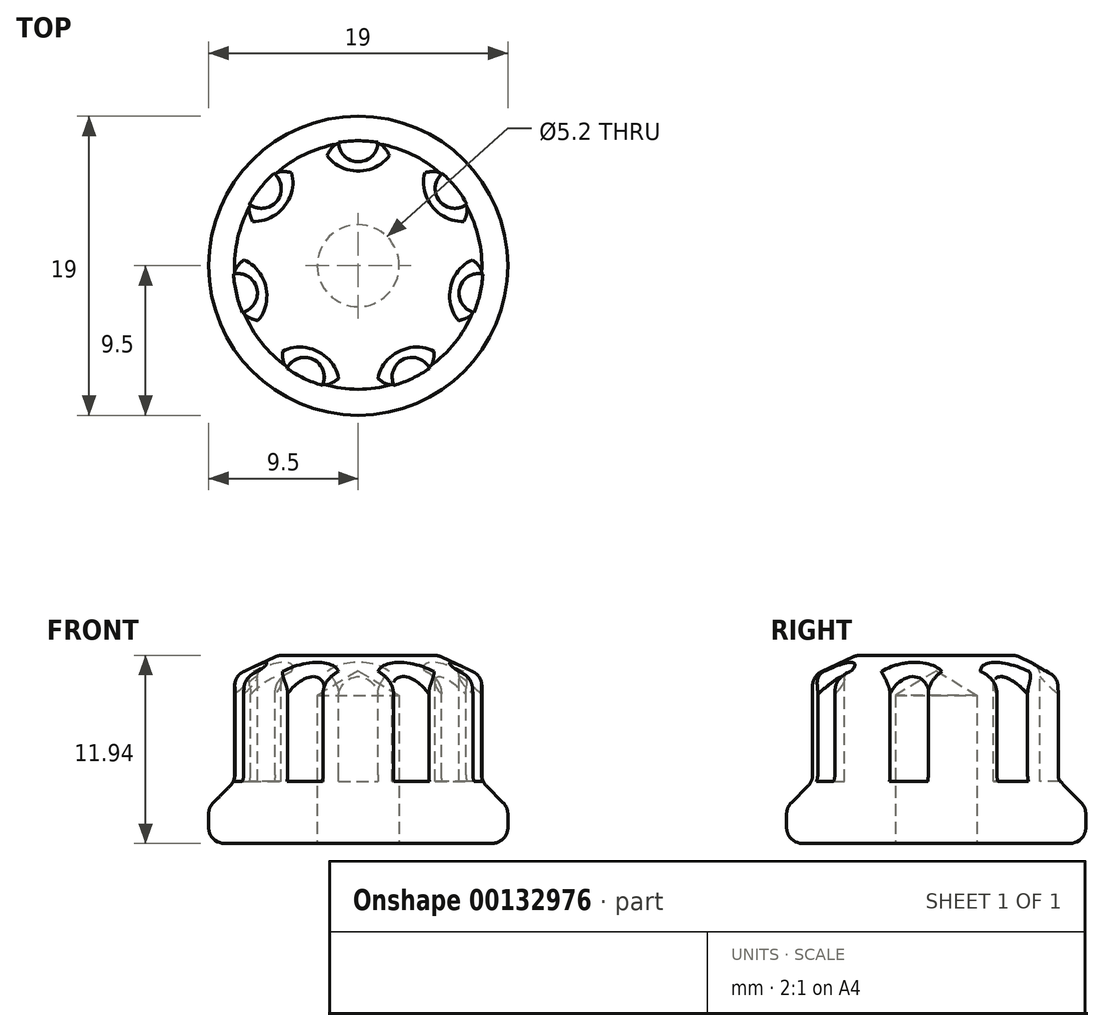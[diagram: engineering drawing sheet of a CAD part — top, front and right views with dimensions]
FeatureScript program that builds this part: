
annotation { "Feature Type Name" : "Feature", "Feature Type Description" : "" }
export const myFeature = defineFeature(function(context is Context, id is Id, definition is map)
    precondition{}
    {
        {
            var Q0;
            Q0=qCreatedBy(makeId("Front.planeOp"),FACE);
            var sketch = newSketch(context, id + "F0", { "sketchPlane" : qUnion([Q0])});
            skLineSegment(sketch, "E0", {"start": v(0, 0) * mm, "end": v(9.5, 0) * mm});
            skLineSegment(sketch, "E1", {"start": v(9.5, 0) * mm, "end": v(9.5, 2.29) * mm});
            skLineSegment(sketch, "E2", {"start": v(7.85, 3.94) * mm, "end": v(9.5, 2.29) * mm});
            skLineSegment(sketch, "E3", {"start": v(7.85, 3.94) * mm, "end": v(7.85, 10.65) * mm});
            skLineSegment(sketch, "E4", {"start": v(7.85, 10.65) * mm, "end": v(5.08, 11.94) * mm});
            skLineSegment(sketch, "E5", {"start": v(5.08, 11.94) * mm, "end": v(0, 11.94) * mm});
            skLineSegment(sketch, "E6", {"start": v(0, 11.94) * mm, "end": v(0, 0) * mm});
            skSolve(sketch);
        }
        {
            var Q0;
            Q0=makeQuery(id+"F0.imprint","IMPRINT",FACE,{"disambiguationData":[TD([[makeQuery(id+"F0.imprint","IMPRINT",EDGE,{"derivedFrom":sQuery(id+"F0.wireOp",EDGE,"E0")}),1.0]])]});
            var Q1;
            Q1=sQuery(id+"F0.wireOp",EDGE,"E6");
            revolve(context, id + "F1", {"entities" : qUnion([Q0]), "axis" : qUnion([Q1]), "revolveType" : RevolveType.FULL});
        }
        {
            var Q0;
            Q0=makeQuery(id+"F1.opRevolve","SWEPT_FACE",FACE,{"disambiguationData":[OSD([sQuery(id+"F0.wireOp",EDGE,"E5")])]});
            var sketch = newSketch(context, id + "F2", { "sketchPlane" : qUnion([Q0])});
            skCircle(sketch, "E7", {"center": v(0, 7.85) * mm, "radius": 1.25 * mm});
            skCircle(sketch, "E8.1.0", {"center": v(-6.14, 4.9) * mm, "radius": 1.25 * mm});
            skCircle(sketch, "E8.2.0", {"center": v(-7.65, -1.75) * mm, "radius": 1.25 * mm});
            skCircle(sketch, "E8.3.0", {"center": v(-3.4, -7.07) * mm, "radius": 1.25 * mm});
            skCircle(sketch, "E8.4.0", {"center": v(3.4, -7.07) * mm, "radius": 1.25 * mm});
            skCircle(sketch, "E8.5.0", {"center": v(7.65, -1.75) * mm, "radius": 1.25 * mm});
            skCircle(sketch, "E8.6.0", {"center": v(6.14, 4.9) * mm, "radius": 1.25 * mm});
            skPoint(sketch, "E8.center", {"position": v(0, 0) * mm});
            skSolve(sketch);
        }
        {
            var Q0;
            Q0=makeQuery(id+"F2.imprint","IMPRINT",FACE,{"disambiguationData":[TD([[makeQuery(id+"F2.imprint","IMPRINT",EDGE,{"derivedFrom":sQuery(id+"F2.wireOp",EDGE,"E8.2.0")}),1.0]])]});
            var Q1;
            Q1=makeQuery(id+"F2.imprint","IMPRINT",FACE,{"disambiguationData":[TD([[makeQuery(id+"F2.imprint","IMPRINT",EDGE,{"derivedFrom":sQuery(id+"F2.wireOp",EDGE,"E8.1.0")}),1.0]])]});
            var Q2;
            Q2=makeQuery(id+"F2.imprint","IMPRINT",FACE,{"disambiguationData":[TD([[makeQuery(id+"F2.imprint","IMPRINT",EDGE,{"derivedFrom":sQuery(id+"F2.wireOp",EDGE,"E7")}),1.0]])]});
            var Q3;
            Q3=makeQuery(id+"F2.imprint","IMPRINT",FACE,{"disambiguationData":[TD([[makeQuery(id+"F2.imprint","IMPRINT",EDGE,{"derivedFrom":sQuery(id+"F2.wireOp",EDGE,"E8.6.0")}),1.0]])]});
            var Q4;
            Q4=makeQuery(id+"F2.imprint","IMPRINT",FACE,{"disambiguationData":[TD([[makeQuery(id+"F2.imprint","IMPRINT",EDGE,{"derivedFrom":sQuery(id+"F2.wireOp",EDGE,"E8.5.0")}),1.0]])]});
            var Q5;
            Q5=makeQuery(id+"F2.imprint","IMPRINT",FACE,{"disambiguationData":[TD([[makeQuery(id+"F2.imprint","IMPRINT",EDGE,{"derivedFrom":sQuery(id+"F2.wireOp",EDGE,"E8.4.0")}),1.0]])]});
            var Q6;
            Q6=makeQuery(id+"F2.imprint","IMPRINT",FACE,{"disambiguationData":[TD([[makeQuery(id+"F2.imprint","IMPRINT",EDGE,{"derivedFrom":sQuery(id+"F2.wireOp",EDGE,"E8.3.0")}),1.0]])]});
            extrude(context, id + "F3", {"entities" : qUnion([Q0, Q1, Q2, Q3, Q4, Q5, Q6]), "operationType" : NewBodyOperationType.REMOVE, "oppositeDirection" : true, "depth" : 8 * mm});
        }
        {
            var Q0;
            Q0=makeQuery(id+"F1.opRevolve","SWEPT_EDGE",EDGE,{"disambiguationData":[OSD([sQuery(id+"F0.wireOp",EDGE,"E2"),sQuery(id+"F0.wireOp",EDGE,"E3")])]});
            var Q1;
            Q1=makeQuery(id+"F1.opRevolve","SWEPT_EDGE",EDGE,{"disambiguationData":[OSD([sQuery(id+"F0.wireOp",EDGE,"E1"),sQuery(id+"F0.wireOp",EDGE,"E2")])]});
            var Q2;
            Q2=makeQuery(id+"F1.opRevolve","SWEPT_EDGE",EDGE,{"disambiguationData":[OSD([sQuery(id+"F0.wireOp",EDGE,"E0"),sQuery(id+"F0.wireOp",EDGE,"E1")])]});
            var Q3;
            Q3=makeQuery(id+"F1.opRevolve","SWEPT_FACE",FACE,{"disambiguationData":[OSD([sQuery(id+"F0.wireOp",EDGE,"E4")])]});
            fillet(context, id + "F4", {"entities" : qUnion([Q0, Q1, Q2, Q3]), "radius" : 1 * mm, "tangentPropagation" : true, "allowEdgeOverflow" : false});
        }
        {
            var Q0;
            Q0=makeQuery(id+"F1.opRevolve","SWEPT_FACE",FACE,{"disambiguationData":[OSD([sQuery(id+"F0.wireOp",EDGE,"E0")])]});
            var sketch = newSketch(context, id + "F5", { "sketchPlane" : qUnion([Q0])});
            skPoint(sketch, "E9", {"position": v(0, 0) * mm});
            skSolve(sketch);
        }
        {
            var Q0;
            Q0=sQuery(id+"F5.wireOp",VERTEX,"E9");
            var Q1;
            Q1=makeQuery(id+"F1.opRevolve","SWEPT_BODY",BODY,{"disambiguationData":[OSD([sQuery(id+"F0.wireOp",EDGE,"E0"),sQuery(id+"F0.wireOp",EDGE,"E1"),sQuery(id+"F0.wireOp",EDGE,"E2"),sQuery(id+"F0.wireOp",EDGE,"E3"),sQuery(id+"F0.wireOp",EDGE,"E4"),sQuery(id+"F0.wireOp",EDGE,"E5"),sQuery(id+"F0.wireOp",EDGE,"E6")])]});
            hole(context, id + "F6", {"style" : HoleStyle.SIMPLE, "endStyle" : HoleEndStyle.BLIND, "holeDiameter" : (1.6 * 2) * mm, "holeDepth" : 5 * mm, "locations" : qUnion([Q0]), "scope" : qUnion([Q1])});
        }
        {
            var Q0;
            Q0=sQuery(id+"F5.wireOp",VERTEX,"E9");
            var Q1;
            Q1=makeQuery(id+"F1.opRevolve","SWEPT_BODY",BODY,{"disambiguationData":[OSD([sQuery(id+"F0.wireOp",EDGE,"E0"),sQuery(id+"F0.wireOp",EDGE,"E1"),sQuery(id+"F0.wireOp",EDGE,"E2"),sQuery(id+"F0.wireOp",EDGE,"E3"),sQuery(id+"F0.wireOp",EDGE,"E4"),sQuery(id+"F0.wireOp",EDGE,"E5"),sQuery(id+"F0.wireOp",EDGE,"E6")])]});
            hole(context, id + "F7", {"style" : HoleStyle.SIMPLE, "endStyle" : HoleEndStyle.BLIND, "holeDiameter" : (2.6 * 2) * mm, "holeDepth" : 9.4 * mm, "locations" : qUnion([Q0]), "scope" : qUnion([Q1])});
        }
    });
